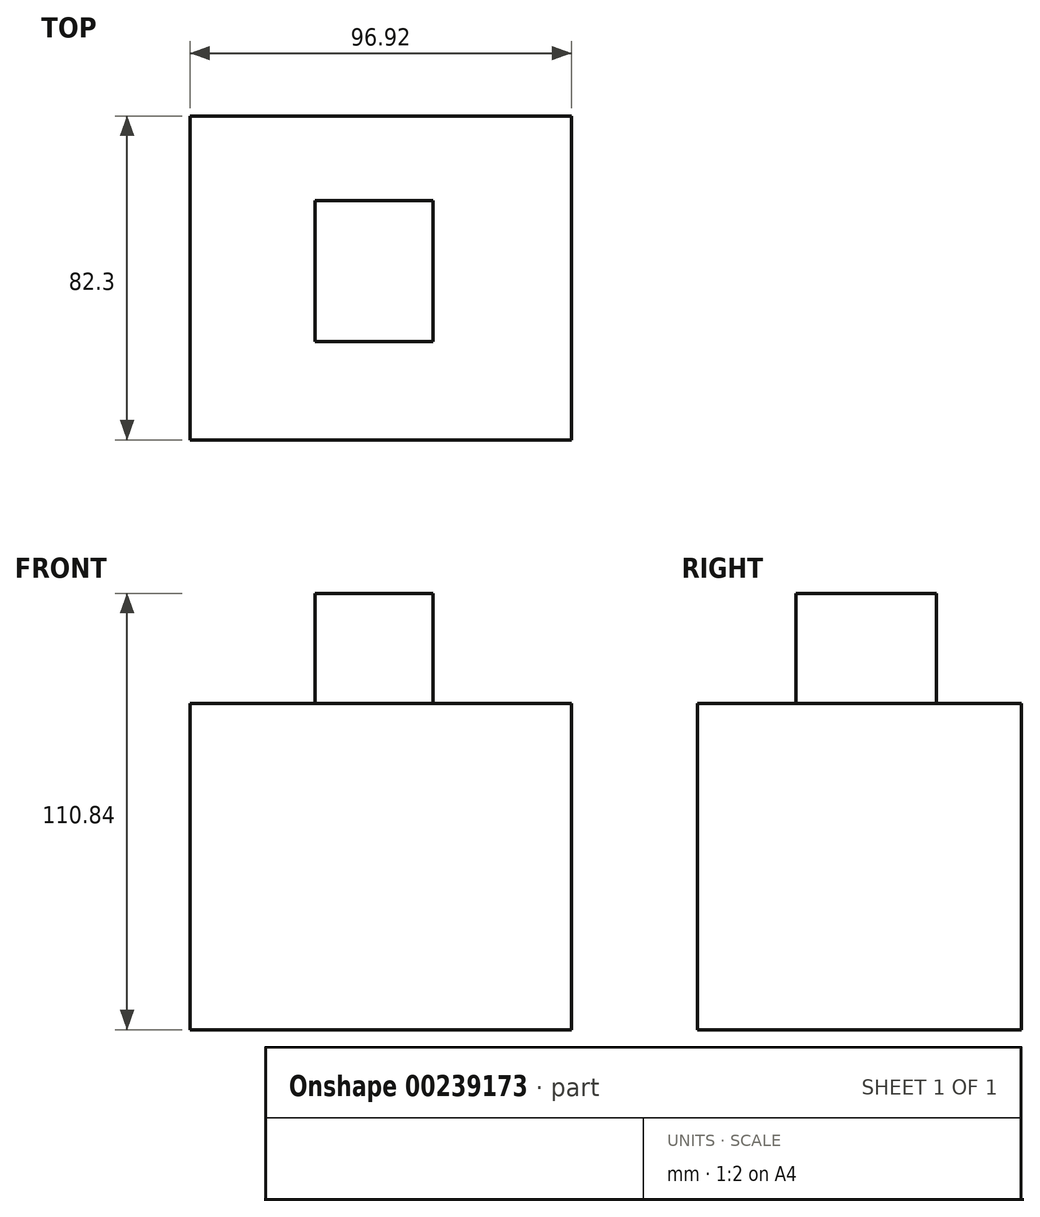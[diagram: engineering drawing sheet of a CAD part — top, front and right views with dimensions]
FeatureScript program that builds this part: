
annotation { "Feature Type Name" : "Feature", "Feature Type Description" : "" }
export const myFeature = defineFeature(function(context is Context, id is Id, definition is map)
    precondition{}
    {
        {
            var Q0;
            Q0=qCreatedBy(makeId("Front.planeOp"),FACE);
            var sketch = newSketch(context, id + "F0", { "sketchPlane" : qUnion([Q0])});
            skLineSegment(sketch, "E0.bottom", {"start": v(-48.33, 44.02) * mm, "end": v(48.6, 44.02) * mm});
            skLineSegment(sketch, "E0.top", {"start": v(-48.33, -38.88) * mm, "end": v(48.6, -38.88) * mm});
            skLineSegment(sketch, "E0.left", {"start": v(-48.33, 44.02) * mm, "end": v(-48.33, -38.88) * mm});
            skLineSegment(sketch, "E0.right", {"start": v(48.6, 44.02) * mm, "end": v(48.6, -38.88) * mm});
            skSolve(sketch);
        }
        {
            var Q0;
            Q0 = qSketchRegion(id + "F0", true);
            extrude(context, id + "F1", {"entities" : qUnion([Q0]), "endBound" : BoundingType.SYMMETRIC, "depth" : 82.3 * mm});
        }
        {
            var Q0;
            Q0=makeQuery(id+"F1.opExtrude","SWEPT_FACE",FACE,{"disambiguationData":[OSD([sQuery(id+"F0.wireOp",EDGE,"E0.bottom")])]});
            var sketch = newSketch(context, id + "F2", { "sketchPlane" : qUnion([Q0])});
            skLineSegment(sketch, "E1.bottom", {"start": v(-16.61, 19.6) * mm, "end": v(13.36, 19.6) * mm});
            skLineSegment(sketch, "E1.top", {"start": v(-16.61, -16.1) * mm, "end": v(13.36, -16.1) * mm});
            skLineSegment(sketch, "E1.left", {"start": v(-16.61, 19.6) * mm, "end": v(-16.61, -16.1) * mm});
            skLineSegment(sketch, "E1.right", {"start": v(13.36, 19.6) * mm, "end": v(13.36, -16.1) * mm});
            skSolve(sketch);
        }
        {
            var Q0;
            Q0 = qSketchRegion(id + "F2", true);
            extrude(context, id + "F3", {"entities" : qUnion([Q0]), "operationType" : NewBodyOperationType.ADD, "depth" : 27.94 * mm});
        }
    });
